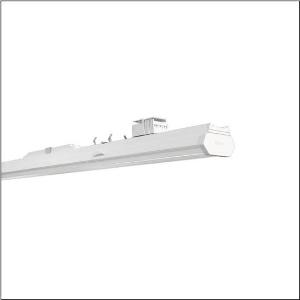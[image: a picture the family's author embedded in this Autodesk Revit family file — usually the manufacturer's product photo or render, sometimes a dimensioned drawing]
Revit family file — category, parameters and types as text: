
# Revit family: licross_r__21_protected_ho_52td12dn4e5md_1fe0
name_source: partatom
category: Lighting Fixtures
units: mm (PartAtom-declared; Revit-internal decimal feet)

## family parameters
Cut with Voids When Loaded = No
Host = Face
Light Source = No
Part Type = Normal
Room Calculation Point = No
Round Connector Dimension = Use Diameter
Shared = No

## types (1)
- --- (1 x LED, 2200 lm, 14.2 W, 4000K)
    Apparent Load = 14 VA
    CIE Flux Codes = 70 91 97 98 100
    Color Rendering = 80
    Color Temperature = 4000K
    Default Elevation = 1800 mm
    Description = Licross® 21 Protected HO, luminaire insert, of sheet steel, galvanised, coil coated, white, length: 1.500mm, width: 90mm, height: 103mm, LED rated luminous flux: 14.690lm, light colour: 840, control gear: DALI 2, with plug, 6-pole, with phase selection, mains connection: 220..240V, AC/DC, 0/50..60Hz, rated input power: 85W, without changeover relay, for emergency light function, for central battery installations according to DIN EN 60598-2-22, halogen-free wiring, primary light control with lens, of plastic, primary optical cover: cover, of PMMA, light emission: direct distribution, primary light characteristic: symmetric, protection rating (complete): IP54, insulation class (complete): insulation class I (protective earthing), certification: CE, ENEC, VDE, UKCA, protection symbol: D if used in an environment with non-conductive dust loads with corresponding accessories, impact resistance: IK06, permissible ambient temperature for indoor applications: -25..+35°C, standard: EN 60598-2-22, corresponds to IFS (International Featured Standards) requirements for safety and quality in the food industry, reducing of maximum allowable ambient temperature of 5°C with ceiling mounting, LABS conformity tested according to VDMA 24364:2018-05, packaging unit: 1 piece
    Height = 92 mm
    Lamp = 1 x LED
    Lamp Light Flux = 2200 lm
    Lamp Power = 14.2 W
    Lamp count = 1
    Length = 1500 mm
    Luminous efficacy = 155 lm/W
    Manufacturer = Siteco
    ModVariant = No
    Model = 52TD12DN4E5MD
    Mounting Place = Ceiling
    Mounting Type = Pendant
    Number of Poles = 1
    OnlyDefault = Yes
    Power Factor = 1
    Product Name = Licross® 21 Protected HO
    Product group = luminaire insert
    ProductGroupID = 901
    Protection Class = Protection class I
    Protection Degree = IP 54
    RLX_Detail_Level = 1
    RLX_Emergency_Light_Flux = 0 lm
    RLX_Emergency_Type = 0
    RLX_Emergency_Type_DB = No
    RlxData = <blob elided: 24937 chars, md5=08185348>
    Socket = socket
    Standby Power = 0 W
    System Light Flux = 2200 lm
    System Power = 14 W
    Type Comments = : DC mode (central or group accumulator) initial emergency light level
    Type Image = l_1256148.jpg
    URL = http://relux.com
    VarID = @adj_064545
    Voltage = 0 V
    Weight = 0.00 kg
    Width = 88 mm

## geometry (parser evidence)
native form markers: Blend x4, Sweep x12
no freeform markers — native parametric forms only
